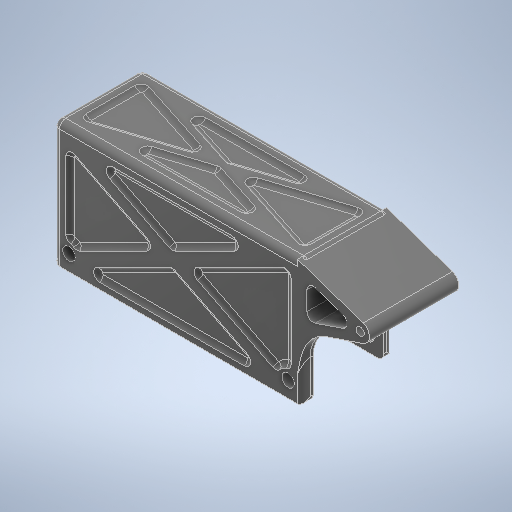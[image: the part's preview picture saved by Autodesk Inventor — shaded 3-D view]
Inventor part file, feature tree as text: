
AUTODESK INVENTOR PART (.ipt)
format: ipt  version: 2025.1 (Build 291241000, 241)  size: 680,960 bytes
history: native  units: mm
features: extrude x11, sketch x11, fillet x7, projected_geometry x7, other x1
ambient origin geometry x8: Origin, YZ Plane, XZ Plane, XY Plane, X Axis, Y Axis, Z Axis, Center Point
bodies: Body1 (feature_tree)
feature tree (37):
  other  "ソリッド1"
  extrude  "押し出し1"  Depth=80.0mm
  extrude  "押し出し2"  Depth=40.0mm
  extrude  "押し出し3"  Depth=3.0mm TaperAngle=0.0deg
  extrude  "押し出し4"  Depth=3.0mm
  extrude  "押し出し5"  Depth=22.5mm TaperAngle=0.0deg
  extrude  "押し出し6"  Depth=25.0mm
  fillet  "フィレット2"  Radius=20.0mm
  extrude  "押し出し7"  Depth=3.0mm TaperAngle=0.0deg
  extrude  "押し出し8"  Depth=15.0mm TaperAngle=0.0deg
  fillet  "フィレット3"  Radius=10.0mm
  extrude  "押し出し9"  Depth=4.0mm
  extrude  "押し出し10"  TaperAngle=0.0deg  [1 undecoded]
  fillet  "フィレット4"  Radius=2.0mm
  fillet  "フィレット5"  Radius=2.6mm
  fillet  "フィレット6"  Radius=6.0mm
  extrude  "押し出し11"  Depth=20.0mm
  fillet  "フィレット7"  Radius=10.0mm
  fillet  "フィレット8"  Radius=24.5mm
  sketch  "スケッチ1"
  sketch  "スケッチ2"
  projected_geometry  "投影ループ1"
  sketch  "スケッチ3"
  projected_geometry  "投影ループ2"
  sketch  "スケッチ4"
  projected_geometry  "投影ループ3"
  projected_geometry  "投影ループ4"
  sketch  "スケッチ5"
  sketch  "スケッチ6"
  sketch  "スケッチ7"
  sketch  "スケッチ8"
  projected_geometry  "投影ループ5"
  sketch  "スケッチ9"
  projected_geometry  "投影ループ6"
  sketch  "スケッチ10"
  projected_geometry  "投影ループ7"
  sketch  "スケッチ11"
note: 1 required parameter value undecoded (feature->parameter linkage not recoverable at this tier; creation-order binding heuristic only, values carry confidence <= 0.55)
